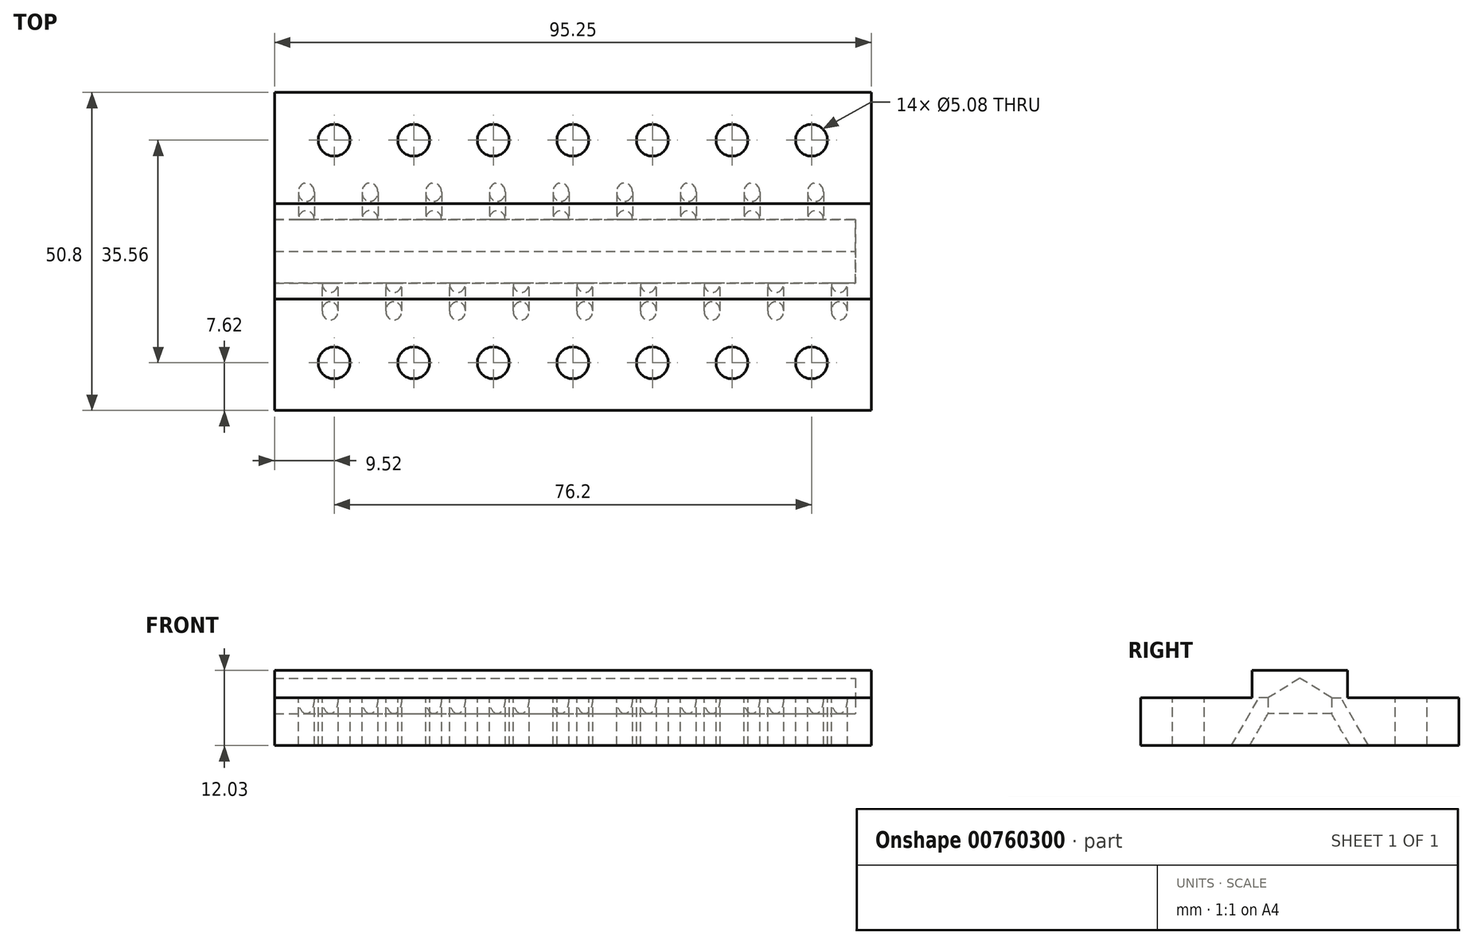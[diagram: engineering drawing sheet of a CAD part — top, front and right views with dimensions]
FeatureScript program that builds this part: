
annotation { "Feature Type Name" : "Feature", "Feature Type Description" : "" }
export const myFeature = defineFeature(function(context is Context, id is Id, definition is map)
    precondition{}
    {
        {
            var Q0;
            Q0=qCreatedBy(makeId("Top.planeOp"),FACE);
            var sketch = newSketch(context, id + "F0", { "sketchPlane" : qUnion([Q0])});
            skLineSegment(sketch, "E0.bottom", {"start": v(47.63, 25.4) * mm, "end": v(-47.63, 25.4) * mm});
            skLineSegment(sketch, "E0.top", {"start": v(47.63, -25.4) * mm, "end": v(-47.62, -25.4) * mm});
            skLineSegment(sketch, "E0.left", {"start": v(47.63, 25.4) * mm, "end": v(47.63, -25.4) * mm});
            skLineSegment(sketch, "E0.right", {"start": v(-47.63, 25.4) * mm, "end": v(-47.62, -25.4) * mm});
            skPoint(sketch, "E0.middle", {"position": v(0, 0) * mm});
            skSolve(sketch);
        }
        {
            var Q0;
            Q0 = qSketchRegion(id + "F0", true);
            extrude(context, id + "F1", {"entities" : qUnion([Q0]), "depth" : 7.62 * mm, "offsetDistance" : 25.4 * mm});
        }
        {
            var Q0;
            Q0=makeQuery(id+"F1.opExtrude","CAP_FACE",FACE,{"disambiguationData":[OSD([sQuery(id+"F0.wireOp",EDGE,"E0.bottom"),sQuery(id+"F0.wireOp",EDGE,"E0.top"),sQuery(id+"F0.wireOp",EDGE,"E0.left"),sQuery(id+"F0.wireOp",EDGE,"E0.right")])],"isStart":false});
            var sketch = newSketch(context, id + "F2", { "sketchPlane" : qUnion([Q0])});
            skCircle(sketch, "E1", {"center": v(-38.1, 17.78) * mm, "radius": 2.54 * mm});
            skCircle(sketch, "E2.MirrorC", {"center": v(-38.1, -17.78) * mm, "radius": 2.54 * mm});
            skCircle(sketch, "E3.1.0.0", {"center": v(-25.4, 17.78) * mm, "radius": 2.54 * mm});
            skCircle(sketch, "E3.1.0.1", {"center": v(-25.4, -17.78) * mm, "radius": 2.54 * mm});
            skCircle(sketch, "E3.2.0.0", {"center": v(-12.7, 17.78) * mm, "radius": 2.54 * mm});
            skCircle(sketch, "E3.2.0.1", {"center": v(-12.7, -17.78) * mm, "radius": 2.54 * mm});
            skCircle(sketch, "E3.3.0.0", {"center": v(0, 17.78) * mm, "radius": 2.54 * mm});
            skCircle(sketch, "E3.3.0.1", {"center": v(0, -17.78) * mm, "radius": 2.54 * mm});
            skCircle(sketch, "E3.4.0.0", {"center": v(12.7, 17.78) * mm, "radius": 2.54 * mm});
            skCircle(sketch, "E3.4.0.1", {"center": v(12.7, -17.78) * mm, "radius": 2.54 * mm});
            skCircle(sketch, "E3.5.0.0", {"center": v(25.4, 17.78) * mm, "radius": 2.54 * mm});
            skCircle(sketch, "E3.5.0.1", {"center": v(25.4, -17.78) * mm, "radius": 2.54 * mm});
            skCircle(sketch, "E3.6.0.0", {"center": v(38.1, 17.78) * mm, "radius": 2.54 * mm});
            skCircle(sketch, "E3.6.0.1", {"center": v(38.1, -17.78) * mm, "radius": 2.54 * mm});
            skLineSegment(sketch, "E3.direction1", {"start": v(-38.1, 17.78) * mm, "end": v(-25.4, 17.78) * mm, "construction": true});
            skSolve(sketch);
        }
        {
            var Q0;
            Q0 = qSketchRegion(id + "F2", true);
            extrude(context, id + "F3", {"entities" : qUnion([Q0]), "operationType" : NewBodyOperationType.REMOVE, "endBound" : BoundingType.THROUGH_ALL, "oppositeDirection" : true, "depth" : 25.4 * mm, "offsetDistance" : 25.4 * mm});
        }
        {
            var Q0;
            Q0=makeQuery(id+"F1.opExtrude","SWEPT_FACE",FACE,{"disambiguationData":[OSD([sQuery(id+"F0.wireOp",EDGE,"E0.left")])]});
            var sketch = newSketch(context, id + "F4", { "sketchPlane" : qUnion([Q0])});
            skLineSegment(sketch, "E4.bottom", {"start": v(5.08, 5.08) * mm, "end": v(-5.08, 5.08) * mm});
            skLineSegment(sketch, "E4.top", {"start": v(5.08, 10.16) * mm, "end": v(-5.08, 10.16) * mm});
            skLineSegment(sketch, "E4.left", {"start": v(5.08, 5.08) * mm, "end": v(5.08, 10.16) * mm});
            skLineSegment(sketch, "E4.right", {"start": v(-5.08, 5.08) * mm, "end": v(-5.08, 10.16) * mm});
            skPoint(sketch, "E4.middle", {"position": v(0, 7.62) * mm});
            skSolve(sketch);
        }
        {
            var Q0;
            Q0 = qSketchRegion(id + "F4", true);
            extrude(context, id + "F5", {"entities" : qUnion([Q0]), "operationType" : NewBodyOperationType.REMOVE, "endBound" : BoundingType.THROUGH_ALL, "oppositeDirection" : true, "depth" : 25.4 * mm, "offsetDistance" : 25.4 * mm});
        }
        {
            var Q0;
            Q0=makeQuery(id+"F5.boolean.opBoolean","COPY",FACE,{"derivedFrom":makeQuery(id+"F5.opExtrude","SWEPT_FACE",FACE,{"disambiguationData":[OSD([sQuery(id+"F4.wireOp",EDGE,"E4.bottom")])]})});
            var Q1;
            Q1=makeQuery(id+"F5.boolean.opBoolean","COPY",EDGE,{"derivedFrom":makeQuery(id+"F5.opExtrude","SWEPT_EDGE",EDGE,{"disambiguationData":[OSD([sQuery(id+"F4.wireOp",EDGE,"E4.bottom"),sQuery(id+"F4.wireOp",EDGE,"E4.left")])]})});
            cPlane(context, id + "F6", {"entities" : qUnion([Q0, Q1]), "cplaneType" : CPlaneType.LINE_ANGLE, "offset" : 25.4 * mm, "angle" : 30 * degree, "width" : 152.4 * mm, "height" : 152.4 * mm});
        }
        {
            var Q0;
            Q0=qCreatedBy(id+"F6.planeOp",FACE);
            cPlane(context, id + "F7", {"entities" : qUnion([Q0]), "cplaneType" : CPlaneType.OFFSET, "offset" : 12.7 * mm, "oppositeDirection" : true, "width" : 152.4 * mm, "height" : 152.4 * mm});
        }
        {
            var Q0;
            Q0=qCreatedBy(id+"F7.planeOp",FACE);
            var sketch = newSketch(context, id + "F8", { "sketchPlane" : qUnion([Q0])});
            skCircle(sketch, "E5", {"center": v(-42.55, -8.2) * mm, "radius": 1.27 * mm});
            skCircle(sketch, "E6.1.0.0", {"center": v(-32.39, -8.2) * mm, "radius": 1.27 * mm});
            skCircle(sketch, "E6.2.0.0", {"center": v(-22.23, -8.2) * mm, "radius": 1.27 * mm});
            skCircle(sketch, "E6.3.0.0", {"center": v(-12.07, -8.2) * mm, "radius": 1.27 * mm});
            skCircle(sketch, "E6.4.0.0", {"center": v(-1.9, -8.2) * mm, "radius": 1.27 * mm});
            skCircle(sketch, "E6.5.0.0", {"center": v(8.25, -8.2) * mm, "radius": 1.27 * mm});
            skCircle(sketch, "E6.6.0.0", {"center": v(18.41, -8.2) * mm, "radius": 1.27 * mm});
            skCircle(sketch, "E6.7.0.0", {"center": v(28.57, -8.2) * mm, "radius": 1.27 * mm});
            skCircle(sketch, "E6.8.0.0", {"center": v(38.73, -8.2) * mm, "radius": 1.27 * mm});
            skCircle(sketch, "E6.9.0.0", {"center": v(48.9, -8.2) * mm, "radius": 1.27 * mm});
            skLineSegment(sketch, "E6.direction1", {"start": v(-42.55, -8.2) * mm, "end": v(-32.39, -8.2) * mm, "construction": true});
            skSolve(sketch);
        }
        {
            var Q0;
            Q0 = qSketchRegion(id + "F8", true);
            extrude(context, id + "F9", {"entities" : qUnion([Q0]), "operationType" : NewBodyOperationType.REMOVE, "endBound" : BoundingType.THROUGH_ALL, "depth" : 25.4 * mm, "offsetDistance" : 25.4 * mm});
        }
        {
            var Q0;
            Q0=makeQuery(id+"F5.boolean.opBoolean","COPY",FACE,{"derivedFrom":makeQuery(id+"F5.opExtrude","SWEPT_FACE",FACE,{"disambiguationData":[OSD([sQuery(id+"F4.wireOp",EDGE,"E4.bottom")])]})});
            var Q1;
            Q1=makeQuery(id+"F5.boolean.opBoolean","INTERSECT",EDGE,{"derivedFrom":[makeQuery(id+"F1.opExtrude","CAP_FACE",FACE,{"disambiguationData":[OSD([sQuery(id+"F0.wireOp",EDGE,"E0.bottom"),sQuery(id+"F0.wireOp",EDGE,"E0.top"),sQuery(id+"F0.wireOp",EDGE,"E0.left"),sQuery(id+"F0.wireOp",EDGE,"E0.right")])],"isStart":false}),makeQuery(id+"F5.opExtrude","SWEPT_FACE",FACE,{"disambiguationData":[OSD([sQuery(id+"F4.wireOp",EDGE,"E4.right")])]})]});
            cPlane(context, id + "F10", {"entities" : qUnion([Q0, Q1]), "cplaneType" : CPlaneType.LINE_ANGLE, "offset" : 25.4 * mm, "angle" : 30 * degree, "width" : 152.4 * mm, "height" : 152.4 * mm});
        }
        {
            var Q0;
            Q0=qCreatedBy(id+"F10.planeOp",FACE);
            cPlane(context, id + "F11", {"entities" : qUnion([Q0]), "cplaneType" : CPlaneType.OFFSET, "offset" : 12.7 * mm, "oppositeDirection" : true, "width" : 152.4 * mm, "height" : 152.4 * mm});
        }
        {
            var Q0;
            Q0=qCreatedBy(id+"F11.planeOp",FACE);
            var sketch = newSketch(context, id + "F12", { "sketchPlane" : qUnion([Q0])});
            skCircle(sketch, "E7", {"center": v(42.55, 8.2) * mm, "radius": 1.27 * mm});
            skCircle(sketch, "E8.1.0.0", {"center": v(32.39, 8.2) * mm, "radius": 1.27 * mm});
            skCircle(sketch, "E8.2.0.0", {"center": v(22.23, 8.2) * mm, "radius": 1.27 * mm});
            skCircle(sketch, "E8.3.0.0", {"center": v(12.07, 8.2) * mm, "radius": 1.27 * mm});
            skCircle(sketch, "E8.4.0.0", {"center": v(1.9, 8.2) * mm, "radius": 1.27 * mm});
            skCircle(sketch, "E8.5.0.0", {"center": v(-8.25, 8.2) * mm, "radius": 1.27 * mm});
            skCircle(sketch, "E8.6.0.0", {"center": v(-18.41, 8.2) * mm, "radius": 1.27 * mm});
            skCircle(sketch, "E8.7.0.0", {"center": v(-28.57, 8.2) * mm, "radius": 1.27 * mm});
            skCircle(sketch, "E8.8.0.0", {"center": v(-38.73, 8.2) * mm, "radius": 1.27 * mm});
            skCircle(sketch, "E8.9.0.0", {"center": v(-48.9, 8.2) * mm, "radius": 1.27 * mm});
            skLineSegment(sketch, "E8.direction1", {"start": v(42.55, 8.2) * mm, "end": v(32.39, 8.2) * mm, "construction": true});
            skSolve(sketch);
        }
        {
            var Q0;
            Q0 = qSketchRegion(id + "F12", true);
            extrude(context, id + "F13", {"entities" : qUnion([Q0]), "operationType" : NewBodyOperationType.REMOVE, "endBound" : BoundingType.THROUGH_ALL, "depth" : 25.4 * mm, "offsetDistance" : 25.4 * mm});
        }
        {
            var Q0;
            Q0=makeQuery(id+"F1.opExtrude","SWEPT_FACE",FACE,{"disambiguationData":[OSD([sQuery(id+"F0.wireOp",EDGE,"E0.left")])]});
            var sketch = newSketch(context, id + "F14", { "sketchPlane" : qUnion([Q0])});
            skLineSegment(sketch, "E9.bottom", {"start": v(-7.62, 7.62) * mm, "end": v(-5.08, 7.62) * mm});
            skLineSegment(sketch, "E9.top", {"start": v(-7.62, 12.03) * mm, "end": v(7.62, 12.03) * mm});
            skLineSegment(sketch, "E9.left", {"start": v(-7.62, 7.62) * mm, "end": v(-7.62, 12.03) * mm});
            skLineSegment(sketch, "E9.right", {"start": v(7.62, 7.62) * mm, "end": v(7.62, 12.03) * mm});
            skLineSegment(sketch, "E10.trimOffspring", {"start": v(5.08, 7.62) * mm, "end": v(7.62, 7.62) * mm});
            skLineSegment(sketch, "E11", {"start": v(-5.08, 7.62) * mm, "end": v(0, 10.76) * mm});
            skLineSegment(sketch, "E12", {"start": v(0, 10.76) * mm, "end": v(5.08, 7.62) * mm});
            skSolve(sketch);
        }
        {
            var Q0;
            Q0 = qSketchRegion(id + "F14", true);
            var Q1;
            Q1=makeQuery(id+"F1.opExtrude","SWEPT_FACE",FACE,{"disambiguationData":[OSD([sQuery(id+"F0.wireOp",EDGE,"E0.right")])]});
            extrude(context, id + "F15", {"entities" : qUnion([Q0]), "operationType" : NewBodyOperationType.ADD, "endBound" : BoundingType.UP_TO_SURFACE, "oppositeDirection" : true, "depth" : 25.4 * mm, "endBoundEntityFace" : qUnion([Q1]), "offsetDistance" : 25.4 * mm});
        }
        {
            var Q0;
            Q0=makeQuery(id+"F5.boolean.opBoolean","COPY",FACE,{"derivedFrom":makeQuery(id+"F5.opExtrude","SWEPT_FACE",FACE,{"disambiguationData":[OSD([sQuery(id+"F4.wireOp",EDGE,"E4.bottom")])]})});
            var sketch = newSketch(context, id + "F16", { "sketchPlane" : qUnion([Q0])});
            skLineSegment(sketch, "E13.bottom", {"start": v(47.63, 5.08) * mm, "end": v(45.09, 5.08) * mm});
            skLineSegment(sketch, "E13.top", {"start": v(47.63, -5.08) * mm, "end": v(45.09, -5.08) * mm});
            skLineSegment(sketch, "E13.left", {"start": v(47.63, 5.08) * mm, "end": v(47.63, -5.08) * mm});
            skLineSegment(sketch, "E13.right", {"start": v(45.09, 5.08) * mm, "end": v(45.09, -5.08) * mm});
            skSolve(sketch);
        }
        {
            var Q0;
            Q0 = qSketchRegion(id + "F16", true);
            extrude(context, id + "F17", {"entities" : qUnion([Q0]), "operationType" : NewBodyOperationType.ADD, "endBound" : BoundingType.UP_TO_NEXT, "depth" : 25.4 * mm, "offsetDistance" : 25.4 * mm});
        }
    });
